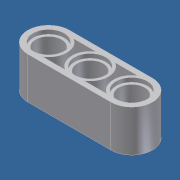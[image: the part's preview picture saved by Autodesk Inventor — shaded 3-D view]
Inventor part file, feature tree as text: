
AUTODESK INVENTOR PART (.ipt)
format: ipt  version: unknown  size: 248,320 bytes
history: native  units: mm
features: extrude x5, sketch x5
ambient origin geometry x8: Origin, YZ Plane, XZ Plane, XY Plane, X Axis, Y Axis, Z Axis, Center Point
bodies: Solid1 (feature_tree)
feature tree (10):
  extrude  "Extrusion1"  Depth=4.0mm
  extrude  "Extrusion6"  TaperAngle=0.0deg  [1 undecoded]
  extrude  "Extrusion7"  TaperAngle=180.0deg  [1 undecoded]
  extrude  "Extrusion8"  Depth=8.0mm TaperAngle=0.0deg
  extrude  "Extrusion9"  Depth=5.0mm
  sketch  "Sketch2"  dims[d0=4.0mm d1=4.0mm]
  sketch  "Sketch7"  dims[d2=16.0mm d3=0.0mm]
  sketch  "Sketch8"  dims[d4=8.0mm d9=180.0deg]
  sketch  "Sketch9"  dims[d10=0.0mm d12=8.0mm d13=0.0mm]
  sketch  "Sketch10"  dims[d56=16.0mm d57=5.0mm d58=10.0mm d60=10.0mm d61=30.0mm d63=8.0mm d65=10.0mm d66=0.0mm d67=6.0mm d68=10.0mm d70=10.0mm d71=30.0mm d73=8.0mm d75=0.8mm d76=0.0mm d77=6.0mm d78=10.0mm d80=10.0mm d81=30.0mm d83=8.0mm d85=0.8mm d86=0.0mm d87=7.0mm d88=7.0mm d89=10.0mm d91=10.0mm d92=20.0mm d94=8.0mm d96=0.8mm d97=0.0mm]
note: 2 required parameter values undecoded (feature->parameter linkage not recoverable at this tier; creation-order binding heuristic only, values carry confidence <= 0.55)
